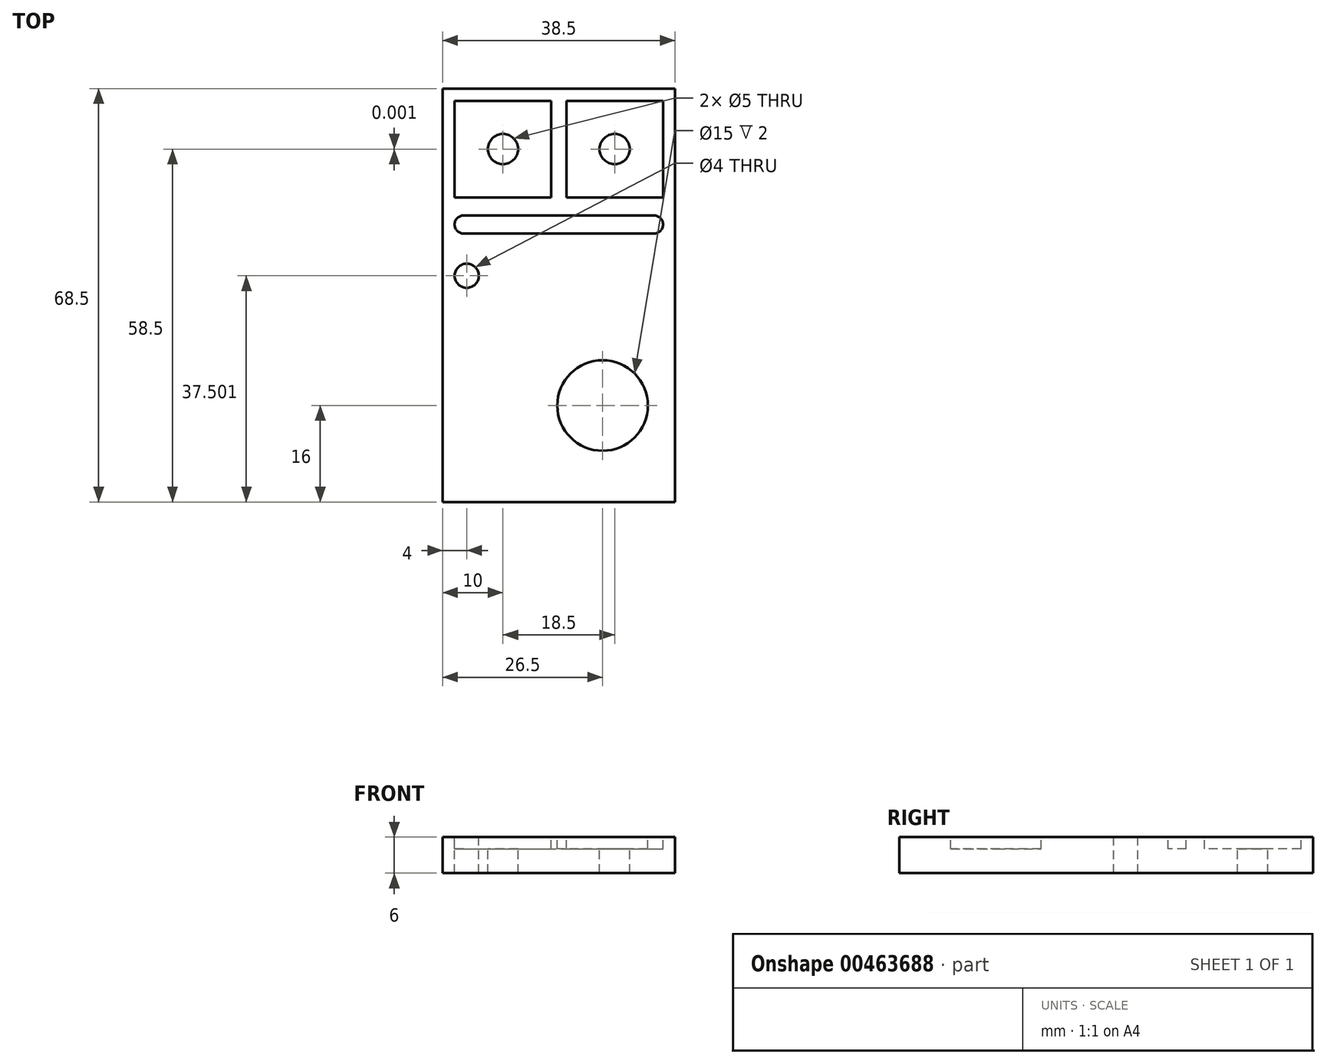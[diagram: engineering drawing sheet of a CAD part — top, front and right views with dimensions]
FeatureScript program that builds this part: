
annotation { "Feature Type Name" : "Feature", "Feature Type Description" : "" }
export const myFeature = defineFeature(function(context is Context, id is Id, definition is map)
    precondition{}
    {
        {
            var Q0;
            Q0=qCreatedBy(makeId("Top.planeOp"),FACE);
            var sketch = newSketch(context, id + "F0", { "sketchPlane" : qUnion([Q0])});
            skLineSegment(sketch, "E0.bottom", {"start": v(-19.25, 34.25) * mm, "end": v(19.25, 34.25) * mm});
            skLineSegment(sketch, "E0.top", {"start": v(-19.25, -34.25) * mm, "end": v(19.25, -34.25) * mm});
            skLineSegment(sketch, "E0.left", {"start": v(-19.25, 34.25) * mm, "end": v(-19.25, -34.25) * mm});
            skLineSegment(sketch, "E0.right", {"start": v(19.25, 34.25) * mm, "end": v(19.25, -34.25) * mm});
            skPoint(sketch, "E0.middle", {"position": v(0, 0) * mm});
            skSolve(sketch);
        }
        {
            var Q0;
            Q0 = qSketchRegion(id + "F0", true);
            extrude(context, id + "F1", {"entities" : qUnion([Q0]), "depth" : 6 * mm});
        }
        {
            var Q0;
            Q0=makeQuery(id+"F1.opExtrude","CAP_FACE",FACE,{"disambiguationData":[OSD([sQuery(id+"F0.wireOp",EDGE,"E0.bottom"),sQuery(id+"F0.wireOp",EDGE,"E0.top"),sQuery(id+"F0.wireOp",EDGE,"E0.left"),sQuery(id+"F0.wireOp",EDGE,"E0.right")])],"isStart":false});
            var sketch = newSketch(context, id + "F2", { "sketchPlane" : qUnion([Q0])});
            skLineSegment(sketch, "E1.bottom", {"start": v(-17.25, 32.25) * mm, "end": v(-1.25, 32.25) * mm});
            skLineSegment(sketch, "E1.top", {"start": v(-17.25, 16.25) * mm, "end": v(-1.25, 16.25) * mm});
            skLineSegment(sketch, "E1.left", {"start": v(-17.25, 32.25) * mm, "end": v(-17.25, 16.25) * mm});
            skLineSegment(sketch, "E1.right", {"start": v(-1.25, 32.25) * mm, "end": v(-1.25, 16.25) * mm});
            skLineSegment(sketch, "E2.bottom", {"start": v(1.25, 32.25) * mm, "end": v(17.25, 32.25) * mm});
            skLineSegment(sketch, "E2.top", {"start": v(1.25, 16.25) * mm, "end": v(17.25, 16.25) * mm});
            skLineSegment(sketch, "E2.left", {"start": v(1.25, 32.25) * mm, "end": v(1.25, 16.25) * mm});
            skLineSegment(sketch, "E2.right", {"start": v(17.25, 32.25) * mm, "end": v(17.25, 16.25) * mm});
            skLineSegment(sketch, "E3", {"start": v(-19.25, 25.57) * mm, "end": v(-17.25, 25.57) * mm, "construction": true});
            skLineSegment(sketch, "E4", {"start": v(17.25, 24.25) * mm, "end": v(19.25, 24.25) * mm, "construction": true});
            skLineSegment(sketch, "E5", {"start": v(-9.18, 34.25) * mm, "end": v(-9.25, 32.25) * mm, "construction": true});
            skLineSegment(sketch, "E6", {"start": v(11.67, 34.25) * mm, "end": v(11.67, 32.25) * mm, "construction": true});
            skSolve(sketch);
        }
        {
            var Q0;
            Q0=makeQuery(id+"F2.imprint","IMPRINT",FACE,{"disambiguationData":[TD([[makeQuery(id+"F2.imprint","IMPRINT",EDGE,{"derivedFrom":sQuery(id+"F2.wireOp",EDGE,"E1.bottom")}),-1.0]])]});
            var Q1;
            Q1=makeQuery(id+"F2.imprint","IMPRINT",FACE,{"disambiguationData":[TD([[makeQuery(id+"F2.imprint","IMPRINT",EDGE,{"derivedFrom":sQuery(id+"F2.wireOp",EDGE,"E2.bottom")}),-1.0]])]});
            extrude(context, id + "F3", {"entities" : qUnion([Q0, Q1]), "operationType" : NewBodyOperationType.REMOVE, "oppositeDirection" : true, "depth" : 2 * mm});
        }
        {
            var Q0;
            Q0=makeQuery(id+"F1.opExtrude","CAP_FACE",FACE,{"disambiguationData":[OSD([sQuery(id+"F0.wireOp",EDGE,"E0.bottom"),sQuery(id+"F0.wireOp",EDGE,"E0.top"),sQuery(id+"F0.wireOp",EDGE,"E0.left"),sQuery(id+"F0.wireOp",EDGE,"E0.right")])],"isStart":false});
            var sketch = newSketch(context, id + "F4", { "sketchPlane" : qUnion([Q0])});
            skLineSegment(sketch, "E7", {"start": v(-17.25, 16.25) * mm, "end": v(-17.25, 13.25) * mm, "construction": true});
            skLineSegment(sketch, "E8.bottom", {"start": v(-17.25, 13.25) * mm, "end": v(17.25, 13.25) * mm});
            skLineSegment(sketch, "E8.top", {"start": v(-17.25, 10.25) * mm, "end": v(17.25, 10.25) * mm});
            skLineSegment(sketch, "E8.left", {"start": v(-17.25, 13.25) * mm, "end": v(-17.25, 10.25) * mm});
            skLineSegment(sketch, "E8.right", {"start": v(17.25, 13.25) * mm, "end": v(17.25, 10.25) * mm});
            skLineSegment(sketch, "E9", {"start": v(-17.25, 13.25) * mm, "end": v(-15.75, 13.25) * mm, "construction": true});
            skLineSegment(sketch, "E10", {"start": v(17.25, 13.25) * mm, "end": v(15.75, 13.25) * mm, "construction": true});
            skCircle(sketch, "E11", {"center": v(15.75, 11.75) * mm, "radius": 1.5 * mm});
            skPoint(sketch, "E11.second.point", {"position": v(17.25, 11.75) * mm});
            skPoint(sketch, "E11.third.point", {"position": v(15.75, 10.25) * mm});
            skCircle(sketch, "E12", {"center": v(-15.75, 11.75) * mm, "radius": 1.5 * mm});
            skPoint(sketch, "E12.second.point", {"position": v(-17.25, 11.75) * mm});
            skPoint(sketch, "E12.third.point", {"position": v(-15.75, 10.25) * mm});
            skSolve(sketch);
        }
        {
            var Q0;
            {var subQ0=sQuery(id+"F4.wireOp",EDGE,"E12");var subQ1=sQuery(id+"F4.wireOp",EDGE,"E8.bottom");var subQ2=makeQuery(id+"F4.imprint","INTERSECT",VERTEX,{"derivedFrom":[subQ1,subQ0]});Q0=makeQuery(id+"F4.imprint","IMPRINT",FACE,{"disambiguationData":[TD([[makeQuery(id+"F4.imprint","IMPRINT",EDGE,{"disambiguationData":[TD([[subQ2,-1.0]])],"derivedFrom":subQ1}),-1.0]])]});}
            var Q1;
            {var subQ0=sQuery(id+"F4.wireOp",EDGE,"E12");var subQ1=makeQuery(id+"F4.imprint","INTERSECT",VERTEX,{"derivedFrom":[sQuery(id+"F4.wireOp",EDGE,"E8.bottom"),subQ0]});Q1=makeQuery(id+"F4.imprint","IMPRINT",FACE,{"disambiguationData":[TD([[makeQuery(id+"F4.imprint","IMPRINT",EDGE,{"disambiguationData":[TD([[subQ1,-1.0]])],"derivedFrom":subQ0}),1.0]])]});}
            var Q2;
            {var subQ0=sQuery(id+"F4.wireOp",EDGE,"E11");var subQ1=makeQuery(id+"F4.imprint","INTERSECT",VERTEX,{"derivedFrom":[sQuery(id+"F4.wireOp",EDGE,"E8.bottom"),subQ0]});Q2=makeQuery(id+"F4.imprint","IMPRINT",FACE,{"disambiguationData":[TD([[makeQuery(id+"F4.imprint","IMPRINT",EDGE,{"disambiguationData":[TD([[subQ1,1.0]])],"derivedFrom":subQ0}),1.0]])]});}
            extrude(context, id + "F5", {"entities" : qUnion([Q0, Q1, Q2]), "operationType" : NewBodyOperationType.REMOVE, "oppositeDirection" : true, "depth" : 2 * mm});
        }
        {
            var Q0;
            Q0=makeQuery(id+"F1.opExtrude","CAP_FACE",FACE,{"disambiguationData":[OSD([sQuery(id+"F0.wireOp",EDGE,"E0.bottom"),sQuery(id+"F0.wireOp",EDGE,"E0.top"),sQuery(id+"F0.wireOp",EDGE,"E0.left"),sQuery(id+"F0.wireOp",EDGE,"E0.right")])],"isStart":false});
            var sketch = newSketch(context, id + "F6", { "sketchPlane" : qUnion([Q0])});
            skLineSegment(sketch, "E13", {"start": v(7.25, -34.25) * mm, "end": v(7.25, -18.25) * mm, "construction": true});
            skLineSegment(sketch, "E14", {"start": v(7.25, -18.25) * mm, "end": v(19.25, -18.25) * mm, "construction": true});
            skCircle(sketch, "E15", {"center": v(7.25, -18.25) * mm, "radius": 7.5 * mm});
            skSolve(sketch);
        }
        {
            var Q0;
            Q0=makeQuery(id+"F6.imprint","IMPRINT",FACE,{"disambiguationData":[TD([[makeQuery(id+"F6.imprint","IMPRINT",EDGE,{"derivedFrom":sQuery(id+"F6.wireOp",EDGE,"E15")}),1.0]])]});
            extrude(context, id + "F7", {"entities" : qUnion([Q0]), "operationType" : NewBodyOperationType.REMOVE, "oppositeDirection" : true, "depth" : 2 * mm});
        }
        {
            var Q0;
            Q0=makeQuery(id+"F1.opExtrude","CAP_FACE",FACE,{"disambiguationData":[OSD([sQuery(id+"F0.wireOp",EDGE,"E0.bottom"),sQuery(id+"F0.wireOp",EDGE,"E0.top"),sQuery(id+"F0.wireOp",EDGE,"E0.left"),sQuery(id+"F0.wireOp",EDGE,"E0.right")])],"isStart":false});
            var sketch = newSketch(context, id + "F8", { "sketchPlane" : qUnion([Q0])});
            skLineSegment(sketch, "E16", {"start": v(-15.25, 10.25) * mm, "end": v(-15.25, 3.25) * mm, "construction": true});
            skLineSegment(sketch, "E17", {"start": v(-15.25, 3.25) * mm, "end": v(-19.25, 3.25) * mm, "construction": true});
            skCircle(sketch, "E18", {"center": v(-15.25, 3.25) * mm, "radius": 2 * mm});
            skSolve(sketch);
        }
        {
            var Q0;
            Q0=makeQuery(id+"F8.imprint","IMPRINT",FACE,{"disambiguationData":[TD([[makeQuery(id+"F8.imprint","IMPRINT",EDGE,{"derivedFrom":sQuery(id+"F8.wireOp",EDGE,"E18")}),1.0]])]});
            var Q1;
            Q1=sQuery(id+"F8.wireOp",EDGE,"E18");
            extrude(context, id + "F9", {"entities" : qUnion([Q0]), "operationType" : NewBodyOperationType.REMOVE, "surfaceEntities" : qUnion([Q1]), "oppositeDirection" : true, "depth" : 8 * mm});
        }
        {
            var Q0;
            Q0=makeQuery(id+"F3.boolean.opBoolean","COPY",FACE,{"derivedFrom":makeQuery(id+"F3.opExtrude","CAP_FACE",FACE,{"disambiguationData":[OSD([sQuery(id+"F2.wireOp",EDGE,"E1.bottom"),sQuery(id+"F2.wireOp",EDGE,"E1.top"),sQuery(id+"F2.wireOp",EDGE,"E1.left"),sQuery(id+"F2.wireOp",EDGE,"E1.right")])],"isStart":false})});
            var sketch = newSketch(context, id + "F10", { "sketchPlane" : qUnion([Q0])});
            skCircle(sketch, "E19", {"center": v(-9.25, 24.25) * mm, "radius": 2.5 * mm});
            skPoint(sketch, "E19.centerSnap0", {"position": v(-9.25, 32.25) * mm});
            skPoint(sketch, "E19.centerSnap1", {"position": v(-17.25, 24.25) * mm});
            skSolve(sketch);
        }
        {
            var Q0;
            Q0 = qSketchRegion(id + "F10", true);
            extrude(context, id + "F11", {"entities" : qUnion([Q0]), "operationType" : NewBodyOperationType.REMOVE, "oppositeDirection" : true, "depth" : 25 * mm, "offsetDistance" : 25 * mm});
        }
        {
            var Q0;
            Q0=makeQuery(id+"F3.boolean.opBoolean","COPY",FACE,{"derivedFrom":makeQuery(id+"F3.opExtrude","CAP_FACE",FACE,{"disambiguationData":[OSD([sQuery(id+"F2.wireOp",EDGE,"E2.bottom"),sQuery(id+"F2.wireOp",EDGE,"E2.top"),sQuery(id+"F2.wireOp",EDGE,"E2.left"),sQuery(id+"F2.wireOp",EDGE,"E2.right")])],"isStart":false})});
            var sketch = newSketch(context, id + "F12", { "sketchPlane" : qUnion([Q0])});
            skCircle(sketch, "E20", {"center": v(9.25, 24.25) * mm, "radius": 2.5 * mm});
            skPoint(sketch, "E20.centerSnap0", {"position": v(9.25, 32.25) * mm});
            skPoint(sketch, "E20.centerSnap1", {"position": v(1.25, 24.25) * mm});
            skSolve(sketch);
        }
        {
            var Q0;
            Q0=makeQuery(id+"F12.imprint","IMPRINT",FACE,{"disambiguationData":[TD([[makeQuery(id+"F12.imprint","IMPRINT",EDGE,{"derivedFrom":sQuery(id+"F12.wireOp",EDGE,"E20")}),1.0]])]});
            extrude(context, id + "F13", {"entities" : qUnion([Q0]), "operationType" : NewBodyOperationType.REMOVE, "oppositeDirection" : true, "depth" : 25 * mm, "offsetDistance" : 25 * mm});
        }
    });
